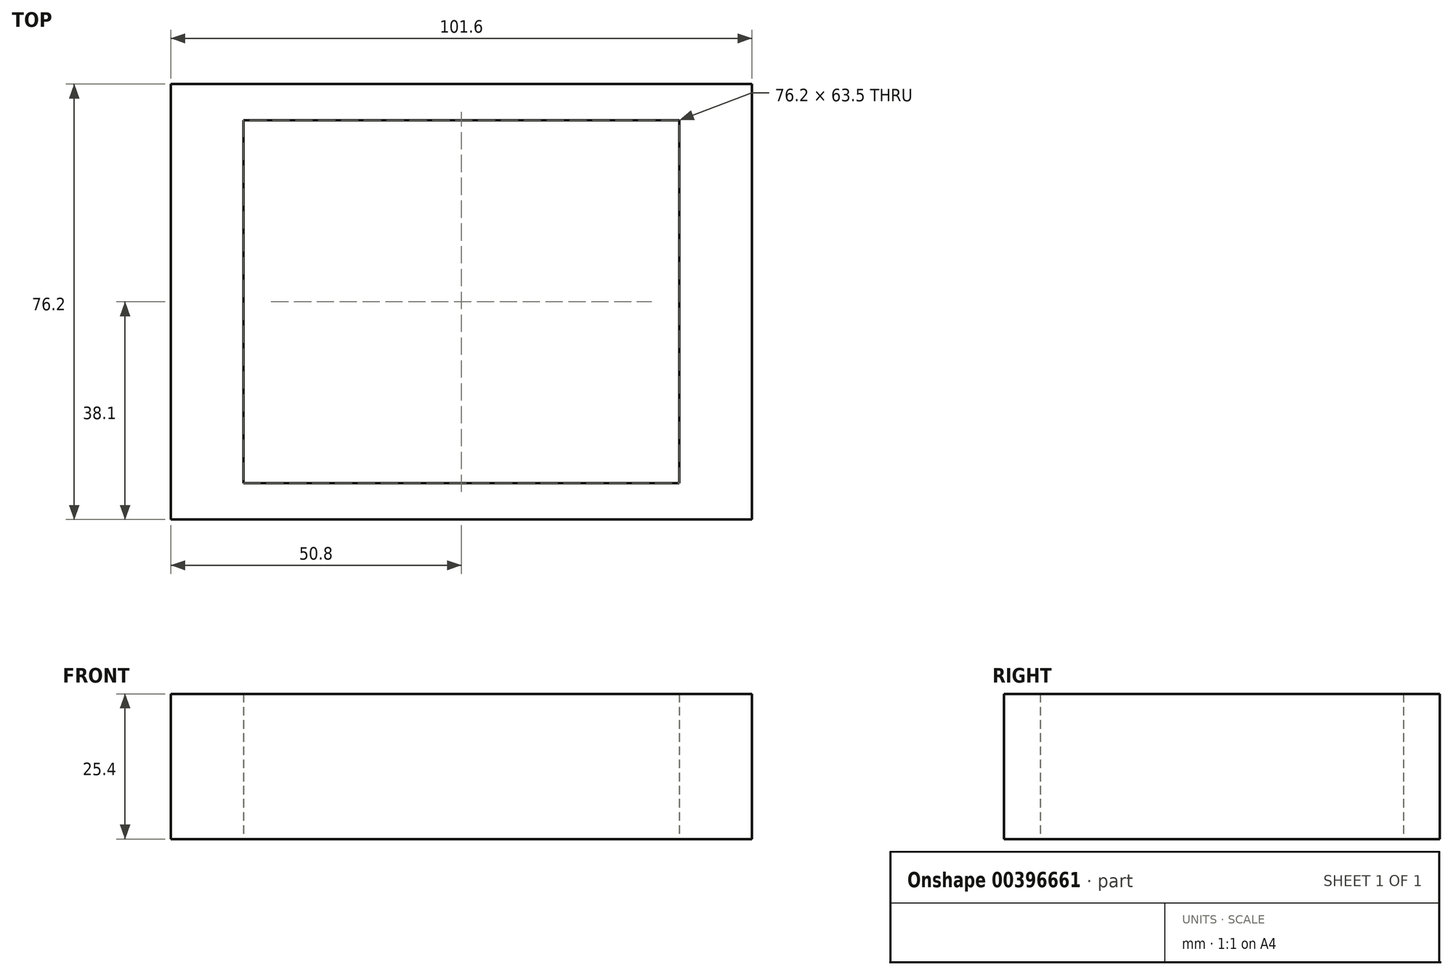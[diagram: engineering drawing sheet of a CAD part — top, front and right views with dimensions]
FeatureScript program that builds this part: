
annotation { "Feature Type Name" : "Feature", "Feature Type Description" : "" }
export const myFeature = defineFeature(function(context is Context, id is Id, definition is map)
    precondition{}
    {
        {
            var Q0;
            Q0=qCreatedBy(makeId("Top.planeOp"),FACE);
            var sketch = newSketch(context, id + "F0", { "sketchPlane" : qUnion([Q0])});
            skLineSegment(sketch, "E0.bottom", {"start": v(-50.8, 38.1) * mm, "end": v(50.8, 38.1) * mm});
            skLineSegment(sketch, "E0.top", {"start": v(-50.8, -38.1) * mm, "end": v(50.8, -38.1) * mm});
            skLineSegment(sketch, "E0.left", {"start": v(-50.8, 38.1) * mm, "end": v(-50.8, -38.1) * mm});
            skLineSegment(sketch, "E0.right", {"start": v(50.8, 38.1) * mm, "end": v(50.8, -38.1) * mm});
            skPoint(sketch, "E0.middle", {"position": v(0, 0) * mm});
            skLineSegment(sketch, "E1.bottom", {"start": v(38.1, 31.75) * mm, "end": v(-38.1, 31.75) * mm});
            skLineSegment(sketch, "E1.top", {"start": v(38.1, -31.75) * mm, "end": v(-38.1, -31.75) * mm});
            skLineSegment(sketch, "E1.left", {"start": v(38.1, 31.75) * mm, "end": v(38.1, -31.75) * mm});
            skLineSegment(sketch, "E1.right", {"start": v(-38.1, 31.75) * mm, "end": v(-38.1, -31.75) * mm});
            skSolve(sketch);
        }
        {
            var Q0;
            Q0 = qSketchRegion(id + "F0", true);
            extrude(context, id + "F1", {"entities" : qUnion([Q0]), "depth" : 25.4 * mm});
        }
    });
